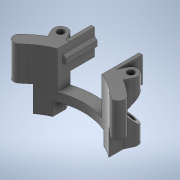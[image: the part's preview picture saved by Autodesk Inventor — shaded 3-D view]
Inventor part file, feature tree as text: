
AUTODESK INVENTOR PART (.ipt)
format: ipt  version: 2020 (Build 240168000, 168)  size: 583,680 bytes
history: native  units: mm
features: sketch x10, extrude x9, projected_geometry x7, other x2, sweep x1
ambient origin geometry x8: Origin, YZ Plane, XZ Plane, XY Plane, X Axis, Y Axis, Z Axis, Center Point
bodies: Body1 (feature_tree)
feature tree (29):
  other  "Твердое тело1"
  extrude  "Выдавливание1"  Depth=35.0mm TaperAngle=0.0deg
  sketch  "Эскиз2"
  extrude  "Выдавливание2"  Depth=4.0mm
  sweep  "Сдвиг1"
  extrude  "Выдавливание5"  Depth=8.0mm
  extrude  "Выдавливание6"  Depth=35.0mm TaperAngle=0.0deg
  extrude  "Выдавливание7"  Depth=8.5mm
  extrude  "Выдавливание8"  TaperAngle=45.0deg  [1 undecoded]
  other  "РабПлоскость1"
  extrude  "Выдавливание9"  Depth=8.5mm
  extrude  "Выдавливание10"  TaperAngle=45.0deg  [1 undecoded]
  extrude  "Выдавливание11"  TaperAngle=0.0deg  [1 undecoded]
  sketch  "Эскиз1"
  sketch  "Эскиз3"
  projected_geometry  "Спроецированная петля1"
  projected_geometry  "Спроецированная петля2"
  sketch  "3D эскиз1"
  sketch  "Эскиз4"
  sketch  "Эскиз6"
  projected_geometry  "Спроецированная петля4"
  sketch  "Эскиз7"
  projected_geometry  "Спроецированная петля5"
  sketch  "Эскиз9"
  projected_geometry  "Спроецированная петля7"
  sketch  "Эскиз11"
  projected_geometry  "Спроецированная петля8"
  sketch  "Эскиз12"
  projected_geometry  "Спроецированная петля9"
note: 3 required parameter values undecoded (feature->parameter linkage not recoverable at this tier; creation-order binding heuristic only, values carry confidence <= 0.55)
